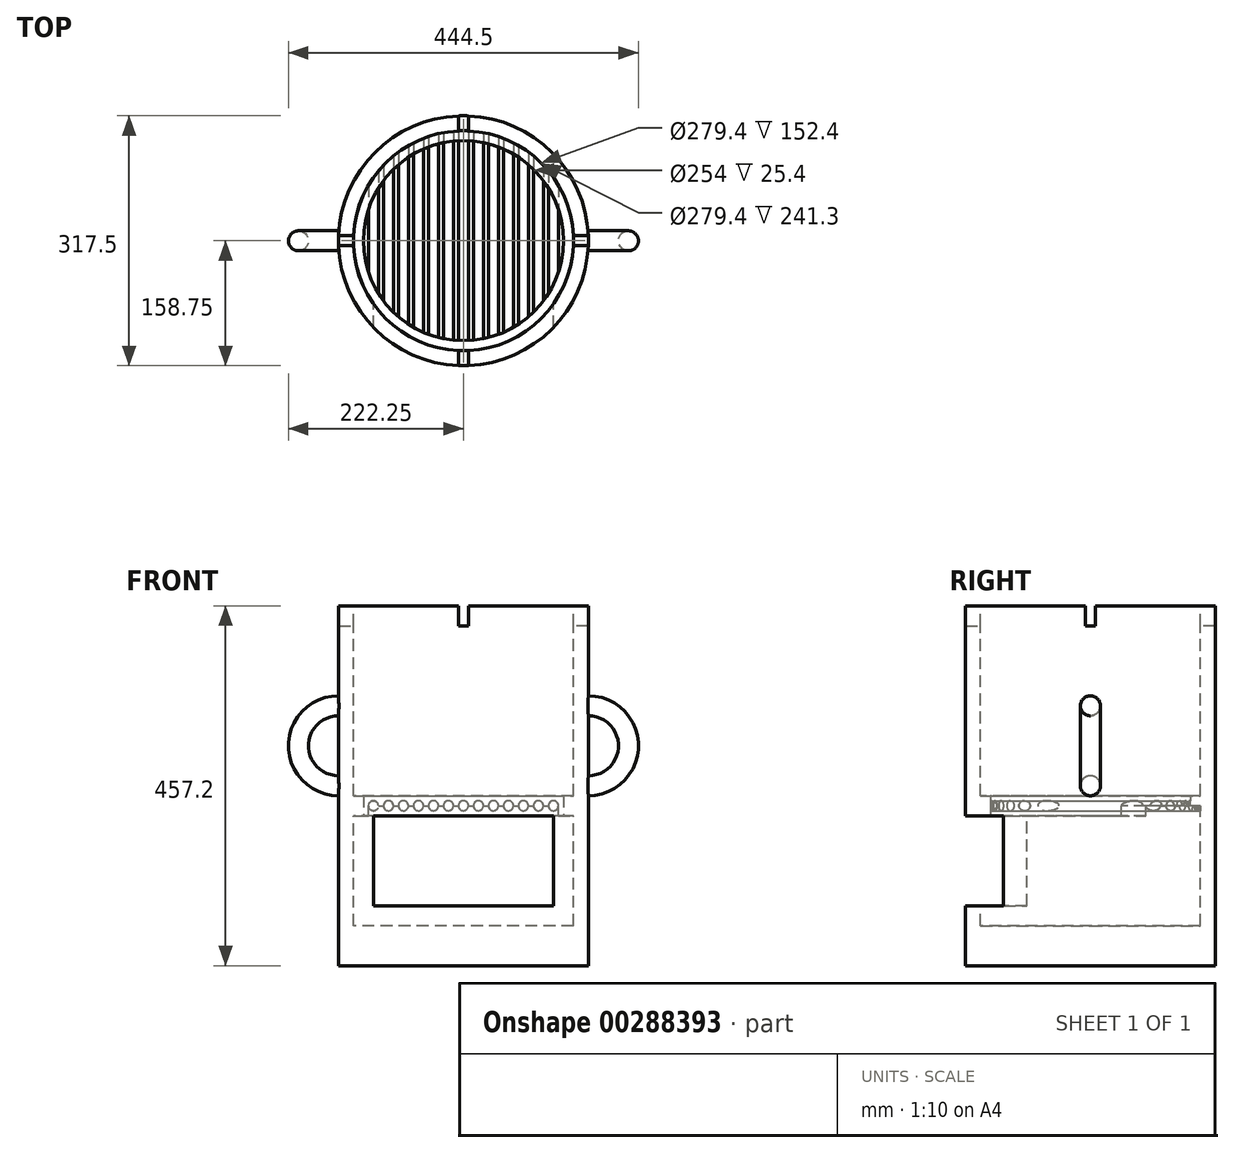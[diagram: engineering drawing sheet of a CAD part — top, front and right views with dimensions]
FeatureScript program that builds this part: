
annotation { "Feature Type Name" : "Feature", "Feature Type Description" : "" }
export const myFeature = defineFeature(function(context is Context, id is Id, definition is map)
    precondition{}
    {
        {
            var Q0;
            Q0=qCreatedBy(makeId("Top.planeOp"),FACE);
            var sketch = newSketch(context, id + "F0", { "sketchPlane" : qUnion([Q0])});
            skCircle(sketch, "E0", {"center": v(0, 0) * mm, "radius": 158.75 * mm});
            skSolve(sketch);
        }
        {
            var Q0;
            Q0=makeQuery(id+"F0.imprint","IMPRINT",FACE,{"disambiguationData":[TD([[makeQuery(id+"F0.imprint","IMPRINT",EDGE,{"derivedFrom":sQuery(id+"F0.wireOp",EDGE,"E0")}),1.0]])]});
            extrude(context, id + "F1", {"entities" : qUnion([Q0]), "depth" : 457.2 * mm});
        }
        {
            var Q0;
            Q0=makeQuery(id+"F1.opExtrude","CAP_FACE",FACE,{"disambiguationData":[OSD([sQuery(id+"F0.wireOp",EDGE,"E0")])],"isStart":false});
            var sketch = newSketch(context, id + "F2", { "sketchPlane" : qUnion([Q0])});
            skPoint(sketch, "E1.0", {"position": v(0, 0) * mm});
            skCircle(sketch, "E2", {"center": v(0, 0) * mm, "radius": 139.7 * mm});
            skSolve(sketch);
        }
        {
            var Q0;
            Q0=makeQuery(id+"F2.imprint","IMPRINT",FACE,{"disambiguationData":[TD([[makeQuery(id+"F2.imprint","IMPRINT",EDGE,{"derivedFrom":sQuery(id+"F2.wireOp",EDGE,"E2")}),1.0]])]});
            extrude(context, id + "F3", {"entities" : qUnion([Q0]), "operationType" : NewBodyOperationType.REMOVE, "oppositeDirection" : true, "depth" : 406.4 * mm});
        }
        {
            var Q0;
            Q0=qCreatedBy(makeId("Front.planeOp"),FACE);
            var sketch = newSketch(context, id + "F4", { "sketchPlane" : qUnion([Q0])});
            skLineSegment(sketch, "E3", {"start": v(-158.75, 0) * mm, "end": v(-158.75, 457.2) * mm});
            skLineSegment(sketch, "E4", {"start": v(158.75, 457.2) * mm, "end": v(158.75, 0) * mm});
            skLineSegment(sketch, "E5", {"start": v(158.75, 457.2) * mm, "end": v(-158.75, 457.2) * mm});
            skLineSegment(sketch, "E6", {"start": v(158.75, 0) * mm, "end": v(-158.75, 0) * mm});
            skPoint(sketch, "E7", {"position": v(0, 0) * mm});
            skLineSegment(sketch, "E8", {"start": v(0, 457.2) * mm, "end": v(0, 0) * mm, "construction": true});
            skLineSegment(sketch, "E9.bottom", {"start": v(114.3, 203.2) * mm, "end": v(-114.3, 203.2) * mm});
            skLineSegment(sketch, "E9.top", {"start": v(114.3, 76.2) * mm, "end": v(-114.3, 76.2) * mm});
            skLineSegment(sketch, "E9.left", {"start": v(114.3, 203.2) * mm, "end": v(114.3, 76.2) * mm});
            skLineSegment(sketch, "E9.right", {"start": v(-114.3, 203.2) * mm, "end": v(-114.3, 76.2) * mm});
            skPoint(sketch, "E10", {"position": v(-514.73, 96.28) * mm});
            skSolve(sketch);
        }
        {
            var Q0;
            Q0=makeQuery(id+"F4.imprint","IMPRINT",FACE,{"disambiguationData":[TD([[makeQuery(id+"F4.imprint","IMPRINT",EDGE,{"derivedFrom":sQuery(id+"F4.wireOp",EDGE,"E9.bottom")}),1.0]])]});
            extrude(context, id + "F5", {"entities" : qUnion([Q0]), "operationType" : NewBodyOperationType.REMOVE, "depth" : 177.8 * mm});
        }
        {
            var Q0;
            Q0=makeQuery(id+"F1.opExtrude","CAP_FACE",FACE,{"disambiguationData":[OSD([sQuery(id+"F0.wireOp",EDGE,"E0")])],"isStart":false});
            var sketch = newSketch(context, id + "F6", { "sketchPlane" : qUnion([Q0])});
            skCircle(sketch, "E11.0.0", {"center": v(0, 0) * mm, "radius": 158.75 * mm, "construction": true});
            skCircle(sketch, "E12.0", {"center": v(0, 0) * mm, "radius": 139.7 * mm, "construction": true});
            skLineSegment(sketch, "E13", {"start": v(-158.75, 0) * mm, "end": v(158.75, 0) * mm, "construction": true});
            skLineSegment(sketch, "E14", {"start": v(0, 158.75) * mm, "end": v(0, -158.75) * mm, "construction": true});
            skLineSegment(sketch, "E15.bottom", {"start": v(-6.35, 158.75) * mm, "end": v(6.35, 158.75) * mm});
            skLineSegment(sketch, "E15.top", {"start": v(-6.35, 139.56) * mm, "end": v(6.35, 139.56) * mm});
            skLineSegment(sketch, "E15.left", {"start": v(-6.35, 158.75) * mm, "end": v(-6.35, 139.56) * mm});
            skLineSegment(sketch, "E15.right", {"start": v(6.35, 158.75) * mm, "end": v(6.35, 139.56) * mm});
            skLineSegment(sketch, "E16.bottom", {"start": v(-158.75, -6.35) * mm, "end": v(-139.56, -6.35) * mm});
            skLineSegment(sketch, "E16.top", {"start": v(-158.75, 6.35) * mm, "end": v(-139.56, 6.35) * mm});
            skLineSegment(sketch, "E16.left", {"start": v(-158.75, -6.35) * mm, "end": v(-158.75, 6.35) * mm});
            skLineSegment(sketch, "E16.right", {"start": v(-139.56, -6.35) * mm, "end": v(-139.56, 6.35) * mm});
            skLineSegment(sketch, "E17.bottom", {"start": v(158.75, 6.35) * mm, "end": v(139.56, 6.35) * mm});
            skLineSegment(sketch, "E17.top", {"start": v(158.75, -6.35) * mm, "end": v(139.56, -6.35) * mm});
            skLineSegment(sketch, "E17.left", {"start": v(158.75, 6.35) * mm, "end": v(158.75, -6.35) * mm});
            skLineSegment(sketch, "E17.right", {"start": v(139.56, 6.35) * mm, "end": v(139.56, -6.35) * mm});
            skLineSegment(sketch, "E18.bottom", {"start": v(6.35, -158.75) * mm, "end": v(-6.35, -158.75) * mm});
            skLineSegment(sketch, "E18.top", {"start": v(6.35, -139.56) * mm, "end": v(-6.35, -139.56) * mm});
            skLineSegment(sketch, "E18.left", {"start": v(6.35, -158.75) * mm, "end": v(6.35, -139.56) * mm});
            skLineSegment(sketch, "E18.right", {"start": v(-6.35, -158.75) * mm, "end": v(-6.35, -139.56) * mm});
            skSolve(sketch);
        }
        {
            var Q0;
            {var subQ0=makeQuery(id+"F1.opExtrude","CAP_EDGE",EDGE,{"disambiguationData":[OSD([sQuery(id+"F0.wireOp",EDGE,"E0")])],"isStart":false});var subQ1=makeQuery(id+"F6.imprint","INTERSECT",VERTEX,{"derivedFrom":[subQ0,sQuery(id+"F6.wireOp",EDGE,"E15.bottom")]});Q0=makeQuery(id+"F6.imprint","IMPRINT",FACE,{"disambiguationData":[TD([[makeQuery(id+"F6.imprint","IMPRINT",EDGE,{"disambiguationData":[TD([[subQ1,-1.0]])],"derivedFrom":subQ0}),1.0]])]});}
            var Q1;
            {var subQ0=sQuery(id+"F6.wireOp",EDGE,"E16.bottom");var subQ1=makeQuery(id+"F1.opExtrude","CAP_EDGE",EDGE,{"disambiguationData":[OSD([sQuery(id+"F0.wireOp",EDGE,"E0")])],"isStart":false});var subQ2=makeQuery(id+"F6.imprint","INTERSECT",VERTEX,{"derivedFrom":[subQ1,subQ0]});Q1=makeQuery(id+"F6.imprint","IMPRINT",FACE,{"disambiguationData":[TD([[makeQuery(id+"F6.imprint","IMPRINT",EDGE,{"disambiguationData":[TD([[subQ2,1.0]])],"derivedFrom":subQ1}),1.0]])]});}
            var Q2;
            {var subQ0=makeQuery(id+"F1.opExtrude","CAP_EDGE",EDGE,{"disambiguationData":[OSD([sQuery(id+"F0.wireOp",EDGE,"E0")])],"isStart":false});var subQ1=makeQuery(id+"F6.imprint","INTERSECT",VERTEX,{"derivedFrom":[subQ0,sQuery(id+"F6.wireOp",EDGE,"E18.bottom")]});Q2=makeQuery(id+"F6.imprint","IMPRINT",FACE,{"disambiguationData":[TD([[makeQuery(id+"F6.imprint","IMPRINT",EDGE,{"disambiguationData":[TD([[subQ1,-1.0]])],"derivedFrom":subQ0}),1.0]])]});}
            var Q3;
            {var subQ0=sQuery(id+"F6.wireOp",EDGE,"E17.bottom");var subQ1=makeQuery(id+"F1.opExtrude","CAP_EDGE",EDGE,{"disambiguationData":[OSD([sQuery(id+"F0.wireOp",EDGE,"E0")])],"isStart":false});var subQ2=makeQuery(id+"F6.imprint","INTERSECT",VERTEX,{"derivedFrom":[subQ1,subQ0]});Q3=makeQuery(id+"F6.imprint","IMPRINT",FACE,{"disambiguationData":[TD([[makeQuery(id+"F6.imprint","IMPRINT",EDGE,{"disambiguationData":[TD([[subQ2,1.0]])],"derivedFrom":subQ1}),1.0]])]});}
            extrude(context, id + "F7", {"entities" : qUnion([Q0, Q1, Q2, Q3]), "operationType" : NewBodyOperationType.REMOVE, "oppositeDirection" : true, "depth" : 25.4 * mm});
        }
        {
            var Q0;
            Q0=makeQuery(id+"F5.boolean.opBoolean","COPY",FACE,{"derivedFrom":makeQuery(id+"F5.opExtrude","SWEPT_FACE",FACE,{"disambiguationData":[OSD([sQuery(id+"F4.wireOp",EDGE,"E9.bottom")])]})});
            var sketch = newSketch(context, id + "F8", { "sketchPlane" : qUnion([Q0])});
            skCircle(sketch, "E19.0.0", {"center": v(0, 0) * mm, "radius": 139.7 * mm});
            skLineSegment(sketch, "E20.0.0", {"start": v(139.56, 6.35) * mm, "end": v(158.62, 6.35) * mm});
            skArc(sketch, "E20.0.1", {"start": v(158.62, 6.35) * mm, "mid": v(158.72, 3.18) * mm, "end": v(158.75, 0) * mm});
            skArc(sketch, "E20.0.2", {"start": v(158.75, 0) * mm, "mid": v(158.72, -3.18) * mm, "end": v(158.62, -6.35) * mm});
            skLineSegment(sketch, "E20.0.3", {"start": v(158.62, -6.35) * mm, "end": v(139.56, -6.35) * mm});
            skArc(sketch, "E20.0.4", {"start": v(139.56, -6.35) * mm, "mid": v(139.7, 0) * mm, "end": v(139.56, 6.35) * mm});
            skLineSegment(sketch, "E21.0.0", {"start": v(6.35, -139.56) * mm, "end": v(6.35, -158.62) * mm});
            skArc(sketch, "E21.0.1", {"start": v(6.35, -158.62) * mm, "mid": v(3.18, -158.72) * mm, "end": v(0, -158.75) * mm});
            skArc(sketch, "E21.0.2", {"start": v(0, -158.75) * mm, "mid": v(-3.18, -158.72) * mm, "end": v(-6.35, -158.62) * mm});
            skLineSegment(sketch, "E21.0.3", {"start": v(-6.35, -158.62) * mm, "end": v(-6.35, -139.56) * mm});
            skArc(sketch, "E21.0.4", {"start": v(-6.35, -139.56) * mm, "mid": v(0, -139.7) * mm, "end": v(6.35, -139.56) * mm});
            skLineSegment(sketch, "E22.0.0", {"start": v(-6.35, 139.56) * mm, "end": v(-6.35, 158.62) * mm});
            skArc(sketch, "E22.0.1", {"start": v(-6.35, 158.62) * mm, "mid": v(-3.18, 158.72) * mm, "end": v(0, 158.75) * mm});
            skArc(sketch, "E22.0.2", {"start": v(0, 158.75) * mm, "mid": v(3.18, 158.72) * mm, "end": v(6.35, 158.62) * mm});
            skLineSegment(sketch, "E22.0.3", {"start": v(6.35, 158.62) * mm, "end": v(6.35, 139.56) * mm});
            skArc(sketch, "E22.0.4", {"start": v(6.35, 139.56) * mm, "mid": v(0, 139.7) * mm, "end": v(-6.35, 139.56) * mm});
            skLineSegment(sketch, "E23.0.0", {"start": v(-139.56, -6.35) * mm, "end": v(-158.62, -6.35) * mm});
            skArc(sketch, "E23.0.1", {"start": v(-158.62, -6.35) * mm, "mid": v(-158.72, -3.18) * mm, "end": v(-158.75, 0) * mm});
            skArc(sketch, "E23.0.2", {"start": v(-158.75, 0) * mm, "mid": v(-158.72, 3.18) * mm, "end": v(-158.62, 6.35) * mm});
            skLineSegment(sketch, "E23.0.3", {"start": v(-158.62, 6.35) * mm, "end": v(-139.56, 6.35) * mm});
            skArc(sketch, "E23.0.4", {"start": v(-139.56, 6.35) * mm, "mid": v(-139.7, 0) * mm, "end": v(-139.56, -6.35) * mm});
            skLineSegment(sketch, "E24", {"start": v(-139.56, 0) * mm, "end": v(139.7, 0) * mm, "construction": true});
            skPoint(sketch, "E24.startSnap0", {"position": v(-139.7, 0) * mm});
            skCircle(sketch, "E25", {"center": v(0, 0) * mm, "radius": 127 * mm});
            skLineSegment(sketch, "E26", {"start": v(0, 127) * mm, "end": v(0, -127) * mm});
            skPoint(sketch, "E27", {"position": v(127, 0) * mm});
            skPoint(sketch, "E28", {"position": v(-127, 0) * mm});
            skPoint(sketch, "E29", {"position": v(-76.2, 0) * mm});
            skPoint(sketch, "E30", {"position": v(-19.05, 0) * mm});
            skPoint(sketch, "E31", {"position": v(-38.1, 0) * mm});
            skPoint(sketch, "E32", {"position": v(-57.15, 0) * mm});
            skPoint(sketch, "E33", {"position": v(-95.25, 0) * mm});
            skPoint(sketch, "E34", {"position": v(-114.3, 0) * mm});
            skLineSegment(sketch, "E35", {"start": v(-114.3, 55.36) * mm, "end": v(-114.3, -55.36) * mm});
            skLineSegment(sketch, "E36", {"start": v(-95.25, 84) * mm, "end": v(-95.25, -84) * mm});
            skLineSegment(sketch, "E37", {"start": v(-76.2, 101.6) * mm, "end": v(-76.2, -101.6) * mm});
            skLineSegment(sketch, "E38", {"start": v(-57.15, -113.41) * mm, "end": v(-57.15, 113.41) * mm});
            skLineSegment(sketch, "E39", {"start": v(-38.1, -121.15) * mm, "end": v(-38.1, 121.15) * mm});
            skLineSegment(sketch, "E40", {"start": v(-19.05, -125.56) * mm, "end": v(-19.05, 125.56) * mm});
            skLineSegment(sketch, "E41.MirrorCS", {"start": v(0, -121.15) * mm, "end": v(0, 121.15) * mm});
            skLineSegment(sketch, "E42.MirrorCS", {"start": v(19.05, -125.56) * mm, "end": v(19.05, 125.56) * mm});
            skLineSegment(sketch, "E43.MirrorCS", {"start": v(38.1, -121.15) * mm, "end": v(38.1, 121.15) * mm});
            skLineSegment(sketch, "E44.MirrorCS", {"start": v(57.15, -113.41) * mm, "end": v(57.15, 113.41) * mm});
            skLineSegment(sketch, "E45.MirrorCS", {"start": v(76.2, 101.6) * mm, "end": v(76.2, -101.6) * mm});
            skLineSegment(sketch, "E46.MirrorCS", {"start": v(95.25, 84) * mm, "end": v(95.25, -84) * mm});
            skLineSegment(sketch, "E47.MirrorCS", {"start": v(114.3, 55.36) * mm, "end": v(114.3, -55.36) * mm});
            skSolve(sketch);
        }
        {
            var Q0;
            {var subQ17=sQuery(id+"F8.wireOp",EDGE,"E19.0.0");var subQ19=makeQuery(id+"F8.imprint","INTERSECT",VERTEX,{"derivedFrom":[subQ17,sQuery(id+"F8.wireOp",EDGE,"E23.0.0")]});Q0=makeQuery(id+"F8.imprint","IMPRINT",FACE,{"disambiguationData":[TD([[makeQuery(id+"F8.imprint","IMPRINT",EDGE,{"disambiguationData":[TD([[subQ19,1.0]])],"derivedFrom":subQ17}),1.0]])]});}
            extrude(context, id + "F9", {"entities" : qUnion([Q0]), "operationType" : NewBodyOperationType.ADD, "oppositeDirection" : true, "depth" : 12.7 * mm});
        }
        {
            var Q0;
            Q0=qCreatedBy(makeId("Front.planeOp"),FACE);
            var sketch = newSketch(context, id + "F10", { "sketchPlane" : qUnion([Q0])});
            skPoint(sketch, "E48.0", {"position": v(-114.3, 203.2) * mm});
            skPoint(sketch, "E49.0", {"position": v(-95.25, 203.2) * mm});
            skPoint(sketch, "E50.0", {"position": v(-76.2, 203.2) * mm});
            skPoint(sketch, "E51.0", {"position": v(-57.15, 203.2) * mm});
            skPoint(sketch, "E52.0", {"position": v(-38.1, 203.2) * mm});
            skPoint(sketch, "E53.0", {"position": v(-19.05, 203.2) * mm});
            skPoint(sketch, "E54.0", {"position": v(0, 203.2) * mm});
            skPoint(sketch, "E55.0", {"position": v(19.05, 203.2) * mm});
            skPoint(sketch, "E56.0", {"position": v(38.1, 203.2) * mm});
            skPoint(sketch, "E57.0", {"position": v(57.15, 203.2) * mm});
            skPoint(sketch, "E58.0", {"position": v(76.2, 203.2) * mm});
            skPoint(sketch, "E59.0", {"position": v(95.25, 203.2) * mm});
            skPoint(sketch, "E60.0", {"position": v(114.3, 203.2) * mm});
            skCircle(sketch, "E61", {"center": v(-114.3, 203.2) * mm, "radius": 6.35 * mm});
            skCircle(sketch, "E62", {"center": v(-95.25, 203.2) * mm, "radius": 6.35 * mm});
            skCircle(sketch, "E63", {"center": v(-76.2, 203.2) * mm, "radius": 6.35 * mm});
            skCircle(sketch, "E64", {"center": v(-57.15, 203.2) * mm, "radius": 6.35 * mm});
            skCircle(sketch, "E65", {"center": v(-38.1, 203.2) * mm, "radius": 6.35 * mm});
            skCircle(sketch, "E66", {"center": v(-19.05, 203.2) * mm, "radius": 6.35 * mm});
            skCircle(sketch, "E67", {"center": v(0, 203.2) * mm, "radius": 6.35 * mm});
            skCircle(sketch, "E68", {"center": v(19.05, 203.2) * mm, "radius": 6.35 * mm});
            skCircle(sketch, "E69", {"center": v(38.1, 203.2) * mm, "radius": 6.35 * mm});
            skCircle(sketch, "E70", {"center": v(57.15, 203.2) * mm, "radius": 6.35 * mm});
            skCircle(sketch, "E71", {"center": v(76.2, 203.2) * mm, "radius": 6.35 * mm});
            skCircle(sketch, "E72", {"center": v(95.25, 203.2) * mm, "radius": 6.35 * mm});
            skCircle(sketch, "E73", {"center": v(114.3, 203.2) * mm, "radius": 6.35 * mm});
            skSolve(sketch);
        }
        {
            var Q0;
            Q0=makeQuery(id+"F10.imprint","IMPRINT",FACE,{"disambiguationData":[TD([[makeQuery(id+"F10.imprint","IMPRINT",EDGE,{"derivedFrom":sQuery(id+"F10.wireOp",EDGE,"E61")}),1.0]])]});
            var Q1;
            Q1=makeQuery(id+"F10.imprint","IMPRINT",FACE,{"disambiguationData":[TD([[makeQuery(id+"F10.imprint","IMPRINT",EDGE,{"derivedFrom":sQuery(id+"F10.wireOp",EDGE,"E66")}),1.0]])]});
            var Q2;
            Q2=makeQuery(id+"F10.imprint","IMPRINT",FACE,{"disambiguationData":[TD([[makeQuery(id+"F10.imprint","IMPRINT",EDGE,{"derivedFrom":sQuery(id+"F10.wireOp",EDGE,"E62")}),1.0]])]});
            var Q3;
            Q3=makeQuery(id+"F10.imprint","IMPRINT",FACE,{"disambiguationData":[TD([[makeQuery(id+"F10.imprint","IMPRINT",EDGE,{"derivedFrom":sQuery(id+"F10.wireOp",EDGE,"E63")}),1.0]])]});
            var Q4;
            Q4=makeQuery(id+"F10.imprint","IMPRINT",FACE,{"disambiguationData":[TD([[makeQuery(id+"F10.imprint","IMPRINT",EDGE,{"derivedFrom":sQuery(id+"F10.wireOp",EDGE,"E65")}),1.0]])]});
            var Q5;
            Q5=makeQuery(id+"F10.imprint","IMPRINT",FACE,{"disambiguationData":[TD([[makeQuery(id+"F10.imprint","IMPRINT",EDGE,{"derivedFrom":sQuery(id+"F10.wireOp",EDGE,"E64")}),1.0]])]});
            var Q6;
            Q6=makeQuery(id+"F10.imprint","IMPRINT",FACE,{"disambiguationData":[TD([[makeQuery(id+"F10.imprint","IMPRINT",EDGE,{"derivedFrom":sQuery(id+"F10.wireOp",EDGE,"E72")}),1.0]])]});
            var Q7;
            Q7=makeQuery(id+"F10.imprint","IMPRINT",FACE,{"disambiguationData":[TD([[makeQuery(id+"F10.imprint","IMPRINT",EDGE,{"derivedFrom":sQuery(id+"F10.wireOp",EDGE,"E71")}),1.0]])]});
            var Q8;
            Q8=makeQuery(id+"F10.imprint","IMPRINT",FACE,{"disambiguationData":[TD([[makeQuery(id+"F10.imprint","IMPRINT",EDGE,{"derivedFrom":sQuery(id+"F10.wireOp",EDGE,"E70")}),1.0]])]});
            var Q9;
            Q9=makeQuery(id+"F10.imprint","IMPRINT",FACE,{"disambiguationData":[TD([[makeQuery(id+"F10.imprint","IMPRINT",EDGE,{"derivedFrom":sQuery(id+"F10.wireOp",EDGE,"E69")}),1.0]])]});
            var Q10;
            Q10=makeQuery(id+"F10.imprint","IMPRINT",FACE,{"disambiguationData":[TD([[makeQuery(id+"F10.imprint","IMPRINT",EDGE,{"derivedFrom":sQuery(id+"F10.wireOp",EDGE,"E68")}),1.0]])]});
            var Q11;
            Q11=makeQuery(id+"F10.imprint","IMPRINT",FACE,{"disambiguationData":[TD([[makeQuery(id+"F10.imprint","IMPRINT",EDGE,{"derivedFrom":sQuery(id+"F10.wireOp",EDGE,"E67")}),1.0]])]});
            var Q12;
            Q12=makeQuery(id+"F10.imprint","IMPRINT",FACE,{"disambiguationData":[TD([[makeQuery(id+"F10.imprint","IMPRINT",EDGE,{"derivedFrom":sQuery(id+"F10.wireOp",EDGE,"E73")}),1.0]])]});
            var Q13;
            Q13=makeQuery(id+"F9.opExtrude","SWEPT_FACE",FACE,{"disambiguationData":[OSD([sQuery(id+"F8.wireOp",EDGE,"E25")])]});
            extrude(context, id + "F11", {"entities" : qUnion([Q0, Q1, Q2, Q3, Q4, Q5, Q6, Q7, Q8, Q9, Q10, Q11, Q12]), "operationType" : NewBodyOperationType.ADD, "endBound" : BoundingType.UP_TO_SURFACE, "endBoundEntityFace" : qUnion([Q13]), "depth" : 228.6 * mm});
        }
        {
            var Q0;
            Q0=makeQuery(id+"F10.imprint","IMPRINT",FACE,{"disambiguationData":[TD([[makeQuery(id+"F10.imprint","IMPRINT",EDGE,{"derivedFrom":sQuery(id+"F10.wireOp",EDGE,"E73")}),1.0]])]});
            var Q1;
            Q1=makeQuery(id+"F10.imprint","IMPRINT",FACE,{"disambiguationData":[TD([[makeQuery(id+"F10.imprint","IMPRINT",EDGE,{"derivedFrom":sQuery(id+"F10.wireOp",EDGE,"E72")}),1.0]])]});
            var Q2;
            Q2=makeQuery(id+"F10.imprint","IMPRINT",FACE,{"disambiguationData":[TD([[makeQuery(id+"F10.imprint","IMPRINT",EDGE,{"derivedFrom":sQuery(id+"F10.wireOp",EDGE,"E71")}),1.0]])]});
            var Q3;
            Q3=makeQuery(id+"F10.imprint","IMPRINT",FACE,{"disambiguationData":[TD([[makeQuery(id+"F10.imprint","IMPRINT",EDGE,{"derivedFrom":sQuery(id+"F10.wireOp",EDGE,"E70")}),1.0]])]});
            var Q4;
            Q4=makeQuery(id+"F10.imprint","IMPRINT",FACE,{"disambiguationData":[TD([[makeQuery(id+"F10.imprint","IMPRINT",EDGE,{"derivedFrom":sQuery(id+"F10.wireOp",EDGE,"E69")}),1.0]])]});
            var Q5;
            Q5=makeQuery(id+"F10.imprint","IMPRINT",FACE,{"disambiguationData":[TD([[makeQuery(id+"F10.imprint","IMPRINT",EDGE,{"derivedFrom":sQuery(id+"F10.wireOp",EDGE,"E68")}),1.0]])]});
            var Q6;
            Q6=makeQuery(id+"F10.imprint","IMPRINT",FACE,{"disambiguationData":[TD([[makeQuery(id+"F10.imprint","IMPRINT",EDGE,{"derivedFrom":sQuery(id+"F10.wireOp",EDGE,"E67")}),1.0]])]});
            var Q7;
            Q7=makeQuery(id+"F10.imprint","IMPRINT",FACE,{"disambiguationData":[TD([[makeQuery(id+"F10.imprint","IMPRINT",EDGE,{"derivedFrom":sQuery(id+"F10.wireOp",EDGE,"E61")}),1.0]])]});
            var Q8;
            Q8=makeQuery(id+"F10.imprint","IMPRINT",FACE,{"disambiguationData":[TD([[makeQuery(id+"F10.imprint","IMPRINT",EDGE,{"derivedFrom":sQuery(id+"F10.wireOp",EDGE,"E66")}),1.0]])]});
            var Q9;
            Q9=makeQuery(id+"F10.imprint","IMPRINT",FACE,{"disambiguationData":[TD([[makeQuery(id+"F10.imprint","IMPRINT",EDGE,{"derivedFrom":sQuery(id+"F10.wireOp",EDGE,"E62")}),1.0]])]});
            var Q10;
            Q10=makeQuery(id+"F10.imprint","IMPRINT",FACE,{"disambiguationData":[TD([[makeQuery(id+"F10.imprint","IMPRINT",EDGE,{"derivedFrom":sQuery(id+"F10.wireOp",EDGE,"E63")}),1.0]])]});
            var Q11;
            Q11=makeQuery(id+"F10.imprint","IMPRINT",FACE,{"disambiguationData":[TD([[makeQuery(id+"F10.imprint","IMPRINT",EDGE,{"derivedFrom":sQuery(id+"F10.wireOp",EDGE,"E65")}),1.0]])]});
            var Q12;
            Q12=makeQuery(id+"F10.imprint","IMPRINT",FACE,{"disambiguationData":[TD([[makeQuery(id+"F10.imprint","IMPRINT",EDGE,{"derivedFrom":sQuery(id+"F10.wireOp",EDGE,"E64")}),1.0]])]});
            extrude(context, id + "F12", {"entities" : qUnion([Q0, Q1, Q2, Q3, Q4, Q5, Q6, Q7, Q8, Q9, Q10, Q11, Q12]), "operationType" : NewBodyOperationType.ADD, "endBound" : BoundingType.UP_TO_NEXT, "oppositeDirection" : true, "depth" : 25.4 * mm});
        }
        {
            var Q0;
            {var subQ0=sQuery(id+"F10.wireOp",EDGE,"E63");var subQ1=sQuery(id+"F8.wireOp",EDGE,"E25");var subQ2=sQuery(id+"F10.wireOp",EDGE,"E73");var subQ3=sQuery(id+"F10.wireOp",EDGE,"E72");var subQ4=sQuery(id+"F10.wireOp",EDGE,"E71");var subQ5=sQuery(id+"F10.wireOp",EDGE,"E69");var subQ6=sQuery(id+"F10.wireOp",EDGE,"E68");var subQ7=sQuery(id+"F10.wireOp",EDGE,"E67");var subQ8=sQuery(id+"F10.wireOp",EDGE,"E66");var subQ9=sQuery(id+"F10.wireOp",EDGE,"E61");var subQ10=sQuery(id+"F10.wireOp",EDGE,"E64");var subQ11=sQuery(id+"F10.wireOp",EDGE,"E70");var subQ12=sQuery(id+"F10.wireOp",EDGE,"E62");var subQ13=sQuery(id+"F10.wireOp",EDGE,"E65");Q0=makeQuery(id+"F12.boolean.opBoolean","SPLIT",FACE,{"disambiguationData":[TD([makeQuery(id+"F1.opExtrude","SWEPT_FACE",FACE,{"disambiguationData":[OSD([sQuery(id+"F0.wireOp",EDGE,"E0")])]}),makeQuery(id+"F3.boolean.opBoolean","COPY",FACE,{"derivedFrom":makeQuery(id+"F3.opExtrude","SWEPT_FACE",FACE,{"disambiguationData":[OSD([sQuery(id+"F2.wireOp",EDGE,"E2")])]})}),makeQuery(id+"F5.boolean.opBoolean","COPY",FACE,{"derivedFrom":makeQuery(id+"F5.opExtrude","SWEPT_FACE",FACE,{"disambiguationData":[OSD([sQuery(id+"F4.wireOp",EDGE,"E9.left")])]})}),makeQuery(id+"F5.boolean.opBoolean","COPY",FACE,{"derivedFrom":makeQuery(id+"F5.opExtrude","SWEPT_FACE",FACE,{"disambiguationData":[OSD([sQuery(id+"F4.wireOp",EDGE,"E9.right")])]})}),makeQuery(id+"F9.opExtrude","SWEPT_FACE",FACE,{"disambiguationData":[OSD([subQ1])]}),makeQuery(id+"F11.opExtrude","SWEPT_FACE",FACE,{"disambiguationData":[OSD([subQ9])]}),makeQuery(id+"F11.opExtrude","SWEPT_FACE",FACE,{"disambiguationData":[OSD([subQ12])]}),makeQuery(id+"F11.opExtrude","SWEPT_FACE",FACE,{"disambiguationData":[OSD([subQ0])]}),makeQuery(id+"F11.opExtrude","SWEPT_FACE",FACE,{"disambiguationData":[OSD([subQ10])]}),makeQuery(id+"F11.opExtrude","SWEPT_FACE",FACE,{"disambiguationData":[OSD([subQ13])]}),makeQuery(id+"F11.opExtrude","SWEPT_FACE",FACE,{"disambiguationData":[OSD([subQ8])]}),makeQuery(id+"F11.opExtrude","SWEPT_FACE",FACE,{"disambiguationData":[OSD([subQ7])]}),makeQuery(id+"F11.opExtrude","SWEPT_FACE",FACE,{"disambiguationData":[OSD([subQ6])]}),makeQuery(id+"F11.opExtrude","SWEPT_FACE",FACE,{"disambiguationData":[OSD([subQ5])]}),makeQuery(id+"F11.opExtrude","SWEPT_FACE",FACE,{"disambiguationData":[OSD([subQ11])]}),makeQuery(id+"F11.opExtrude","SWEPT_FACE",FACE,{"disambiguationData":[OSD([subQ4])]}),makeQuery(id+"F11.opExtrude","SWEPT_FACE",FACE,{"disambiguationData":[OSD([subQ3])]}),makeQuery(id+"F11.opExtrude","SWEPT_FACE",FACE,{"disambiguationData":[OSD([subQ2])]}),makeQuery(id+"F11.opExtrude","CAP_FACE",FACE,{"disambiguationData":[OSD([subQ1]),ownerDisambiguation([makeQuery(id+"F11.opExtrude","SWEPT_BODY",BODY,{"disambiguationData":[OSD([subQ9])]})])],"isStart":false}),makeQuery(id+"F11.opExtrude","CAP_FACE",FACE,{"disambiguationData":[OSD([subQ1]),ownerDisambiguation([makeQuery(id+"F11.opExtrude","SWEPT_BODY",BODY,{"disambiguationData":[OSD([subQ12])]})])],"isStart":false}),makeQuery(id+"F11.opExtrude","CAP_FACE",FACE,{"disambiguationData":[OSD([subQ1]),ownerDisambiguation([makeQuery(id+"F11.opExtrude","SWEPT_BODY",BODY,{"disambiguationData":[OSD([subQ0])]})])],"isStart":false}),makeQuery(id+"F11.opExtrude","CAP_FACE",FACE,{"disambiguationData":[OSD([subQ1]),ownerDisambiguation([makeQuery(id+"F11.opExtrude","SWEPT_BODY",BODY,{"disambiguationData":[OSD([subQ10])]})])],"isStart":false}),makeQuery(id+"F11.opExtrude","CAP_FACE",FACE,{"disambiguationData":[OSD([subQ1]),ownerDisambiguation([makeQuery(id+"F11.opExtrude","SWEPT_BODY",BODY,{"disambiguationData":[OSD([subQ13])]})])],"isStart":false}),makeQuery(id+"F11.opExtrude","CAP_FACE",FACE,{"disambiguationData":[OSD([subQ1]),ownerDisambiguation([makeQuery(id+"F11.opExtrude","SWEPT_BODY",BODY,{"disambiguationData":[OSD([subQ8])]})])],"isStart":false}),makeQuery(id+"F11.opExtrude","CAP_FACE",FACE,{"disambiguationData":[OSD([subQ1]),ownerDisambiguation([makeQuery(id+"F11.opExtrude","SWEPT_BODY",BODY,{"disambiguationData":[OSD([subQ7])]})])],"isStart":false}),makeQuery(id+"F11.opExtrude","CAP_FACE",FACE,{"disambiguationData":[OSD([subQ1]),ownerDisambiguation([makeQuery(id+"F11.opExtrude","SWEPT_BODY",BODY,{"disambiguationData":[OSD([subQ6])]})])],"isStart":false}),makeQuery(id+"F11.opExtrude","CAP_FACE",FACE,{"disambiguationData":[OSD([subQ1]),ownerDisambiguation([makeQuery(id+"F11.opExtrude","SWEPT_BODY",BODY,{"disambiguationData":[OSD([subQ5])]})])],"isStart":false}),makeQuery(id+"F11.opExtrude","CAP_FACE",FACE,{"disambiguationData":[OSD([subQ1]),ownerDisambiguation([makeQuery(id+"F11.opExtrude","SWEPT_BODY",BODY,{"disambiguationData":[OSD([subQ11])]})])],"isStart":false}),makeQuery(id+"F11.opExtrude","CAP_FACE",FACE,{"disambiguationData":[OSD([subQ1]),ownerDisambiguation([makeQuery(id+"F11.opExtrude","SWEPT_BODY",BODY,{"disambiguationData":[OSD([subQ4])]})])],"isStart":false}),makeQuery(id+"F11.opExtrude","CAP_FACE",FACE,{"disambiguationData":[OSD([subQ1]),ownerDisambiguation([makeQuery(id+"F11.opExtrude","SWEPT_BODY",BODY,{"disambiguationData":[OSD([subQ3])]})])],"isStart":false}),makeQuery(id+"F11.opExtrude","CAP_FACE",FACE,{"disambiguationData":[OSD([subQ1]),ownerDisambiguation([makeQuery(id+"F11.opExtrude","SWEPT_BODY",BODY,{"disambiguationData":[OSD([subQ2])]})])],"isStart":false}),makeQuery(id+"F12.opExtrude","SWEPT_FACE",FACE,{"disambiguationData":[OSD([subQ9])]}),makeQuery(id+"F12.opExtrude","SWEPT_FACE",FACE,{"disambiguationData":[OSD([subQ12])]}),makeQuery(id+"F12.opExtrude","SWEPT_FACE",FACE,{"disambiguationData":[OSD([subQ0])]}),makeQuery(id+"F12.opExtrude","SWEPT_FACE",FACE,{"disambiguationData":[OSD([subQ10])]}),makeQuery(id+"F12.opExtrude","SWEPT_FACE",FACE,{"disambiguationData":[OSD([subQ13])]}),makeQuery(id+"F12.opExtrude","SWEPT_FACE",FACE,{"disambiguationData":[OSD([subQ8])]}),makeQuery(id+"F12.opExtrude","SWEPT_FACE",FACE,{"disambiguationData":[OSD([subQ7])]}),makeQuery(id+"F12.opExtrude","SWEPT_FACE",FACE,{"disambiguationData":[OSD([subQ6])]}),makeQuery(id+"F12.opExtrude","SWEPT_FACE",FACE,{"disambiguationData":[OSD([subQ5])]}),makeQuery(id+"F12.opExtrude","SWEPT_FACE",FACE,{"disambiguationData":[OSD([subQ11])]}),makeQuery(id+"F12.opExtrude","SWEPT_FACE",FACE,{"disambiguationData":[OSD([subQ4])]}),makeQuery(id+"F12.opExtrude","SWEPT_FACE",FACE,{"disambiguationData":[OSD([subQ3])]}),makeQuery(id+"F12.opExtrude","SWEPT_FACE",FACE,{"disambiguationData":[OSD([subQ2])]})])],"derivedFrom":makeQuery(id+"F9.boolean.opBoolean","MERGE",FACE,{"derivedFrom":[makeQuery(id+"F5.boolean.opBoolean","COPY",FACE,{"derivedFrom":makeQuery(id+"F5.opExtrude","SWEPT_FACE",FACE,{"disambiguationData":[OSD([sQuery(id+"F4.wireOp",EDGE,"E9.bottom")])]})}),makeQuery(id+"F9.opExtrude","CAP_FACE",FACE,{"disambiguationData":[OSD([sQuery(id+"F8.wireOp",EDGE,"E19.0.0"),subQ1])],"isStart":true})]})});}
            extrude(context, id + "F13", {"entities" : qUnion([Q0]), "operationType" : NewBodyOperationType.ADD, "depth" : 12.7 * mm});
        }
        {
            var Q0;
            Q0=sQuery(id+"F6.wireOp",VERTEX,"E13.start");
            var Q1;
            Q1=qCreatedBy(makeId("Right.planeOp"),FACE);
            cPlane(context, id + "F14", {"entities" : qUnion([Q0, Q1]), "cplaneType" : CPlaneType.PLANE_POINT, "offset" : 25.4 * mm, "width" : 152.4 * mm, "height" : 152.4 * mm});
        }
        {
            var Q0;
            Q0=qCreatedBy(id+"F14.planeOp",FACE);
            var sketch = newSketch(context, id + "F15", { "sketchPlane" : qUnion([Q0])});
            skLineSegment(sketch, "E74", {"start": v(-158.75, 0) * mm, "end": v(-158.75, 431.8) * mm, "construction": true});
            skLineSegment(sketch, "E75", {"start": v(158.75, 431.8) * mm, "end": v(158.75, 0) * mm, "construction": true});
            skLineSegment(sketch, "E76.0", {"start": v(-158.75, 457.2) * mm, "end": v(158.75, 457.2) * mm, "construction": true});
            skLineSegment(sketch, "E77.0", {"start": v(-158.75, 0) * mm, "end": v(158.75, 0) * mm, "construction": true});
            skLineSegment(sketch, "E78.0", {"start": v(158.62, 431.8) * mm, "end": v(158.62, 457.2) * mm, "construction": true});
            skLineSegment(sketch, "E79.0", {"start": v(-158.62, 431.8) * mm, "end": v(-158.62, 457.2) * mm, "construction": true});
            skLineSegment(sketch, "E80", {"start": v(0, 457.2) * mm, "end": v(0, 0) * mm, "construction": true});
            skPoint(sketch, "E81", {"position": v(0, 228.6) * mm});
            skSolve(sketch);
        }
        {
            var Q0;
            Q0=sQuery(id+"F15.wireOp",VERTEX,"E81");
            var Q1;
            Q1=qCreatedBy(id+"F14.planeOp",FACE);
            cPlane(context, id + "F16", {"entities" : qUnion([Q0, Q1]), "cplaneType" : CPlaneType.PLANE_POINT, "offset" : 25.4 * mm, "width" : 152.4 * mm, "height" : 152.4 * mm});
        }
        {
            var Q0;
            Q0=sQuery(id+"F15.wireOp",VERTEX,"E81");
            var Q1;
            Q1=qCreatedBy(makeId("Front.planeOp"),FACE);
            cPlane(context, id + "F17", {"entities" : qUnion([Q0, Q1]), "cplaneType" : CPlaneType.PLANE_POINT, "offset" : 25.4 * mm, "width" : 152.4 * mm, "height" : 152.4 * mm});
        }
        {
            var Q0;
            Q0=qCreatedBy(id+"F17.planeOp",FACE);
            var sketch = newSketch(context, id + "F18", { "sketchPlane" : qUnion([Q0])});
            skPoint(sketch, "E82.0", {"position": v(-158.75, 228.6) * mm});
            skLineSegment(sketch, "E83.0", {"start": v(-158.75, 457.2) * mm, "end": v(-158.75, 0) * mm});
            skArc(sketch, "E84", {"start": v(-158.75, 228.6) * mm, "mid": v(-209.55, 279.4) * mm, "end": v(-158.75, 330.2) * mm});
            skSolve(sketch);
        }
        {
            var Q0;
            Q0=qCreatedBy(id+"F16.planeOp",FACE);
            var sketch = newSketch(context, id + "F19", { "sketchPlane" : qUnion([Q0])});
            skPoint(sketch, "E85.0", {"position": v(0, 228.6) * mm});
            skCircle(sketch, "E86", {"center": v(0, 228.6) * mm, "radius": 12.7 * mm});
            skSolve(sketch);
        }
        {
            var Q0;
            Q0=makeQuery(id+"F19.imprint","IMPRINT",FACE,{"disambiguationData":[TD([[makeQuery(id+"F19.imprint","IMPRINT",EDGE,{"derivedFrom":sQuery(id+"F19.wireOp",EDGE,"E86")}),1.0]])]});
            var Q1;
            Q1=sQuery(id+"F18.wireOp",EDGE,"E84");
            sweep(context, id + "F20", {"profiles" : qUnion([Q0]), "path" : qUnion([Q1])});
        }
        {
            var Q0;
            Q0=makeQuery(id+"F20.opSweep","CAP_FACE",FACE,{"disambiguationData":[OSD([sQuery(id+"F18.wireOp",VERTEX,"E84.end"),sQuery(id+"F19.wireOp",EDGE,"E86")])],"isStart":false});
            var Q1;
            Q1=makeQuery(id+"F20.opSweep","CAP_FACE",FACE,{"disambiguationData":[OSD([sQuery(id+"F18.wireOp",VERTEX,"E84.start"),sQuery(id+"F19.wireOp",EDGE,"E86")])],"isStart":true});
            extrude(context, id + "F21", {"entities" : qUnion([Q0, Q1]), "operationType" : NewBodyOperationType.ADD, "depth" : 12.7 * mm});
        }
        {
            var Q0;
            Q0=makeQuery(id+"F1.opExtrude","SWEPT_BODY",BODY,{"disambiguationData":[OSD([sQuery(id+"F0.wireOp",EDGE,"E0")])]});
            var Q1;
            Q1=qCreatedBy(makeId("Right.planeOp"),FACE);
            mirror(context, id + "F22", {"operationType" : NewBodyOperationType.ADD, "entities" : qUnion([Q0]), "mirrorPlane" : qUnion([Q1])});
        }
        {
            var Q0;
            Q0=sQuery(id+"F18.wireOp",VERTEX,"E82.0");
            var Q1;
            Q1=qCreatedBy(makeId("Top.planeOp"),FACE);
            cPlane(context, id + "F23", {"entities" : qUnion([Q0, Q1]), "cplaneType" : CPlaneType.PLANE_POINT, "offset" : 25.4 * mm, "width" : 152.4 * mm, "height" : 152.4 * mm});
        }
        {
            var Q0;
            Q0=qCreatedBy(id+"F23.planeOp",FACE);
            var sketch = newSketch(context, id + "F24", { "sketchPlane" : qUnion([Q0])});
            skPoint(sketch, "E87.0", {"position": v(-158.75, 0) * mm});
            skCircle(sketch, "E88.0", {"center": v(0, 0) * mm, "radius": 158.75 * mm, "construction": true});
            skArc(sketch, "E89", {"start": v(-126.24, -96.26) * mm, "mid": v(-260.35, 0) * mm, "end": v(-126.24, 96.26) * mm});
            skSolve(sketch);
        }
        {
            var Q0;
            Q0=sQuery(id+"F24.wireOp",VERTEX,"E89.end");
            var Q1;
            Q1=qCreatedBy(makeId("Right.planeOp"),FACE);
            cPlane(context, id + "F25", {"entities" : qUnion([Q0, Q1]), "cplaneType" : CPlaneType.PLANE_POINT, "offset" : 25.4 * mm, "width" : 152.4 * mm, "height" : 152.4 * mm});
        }
    });
